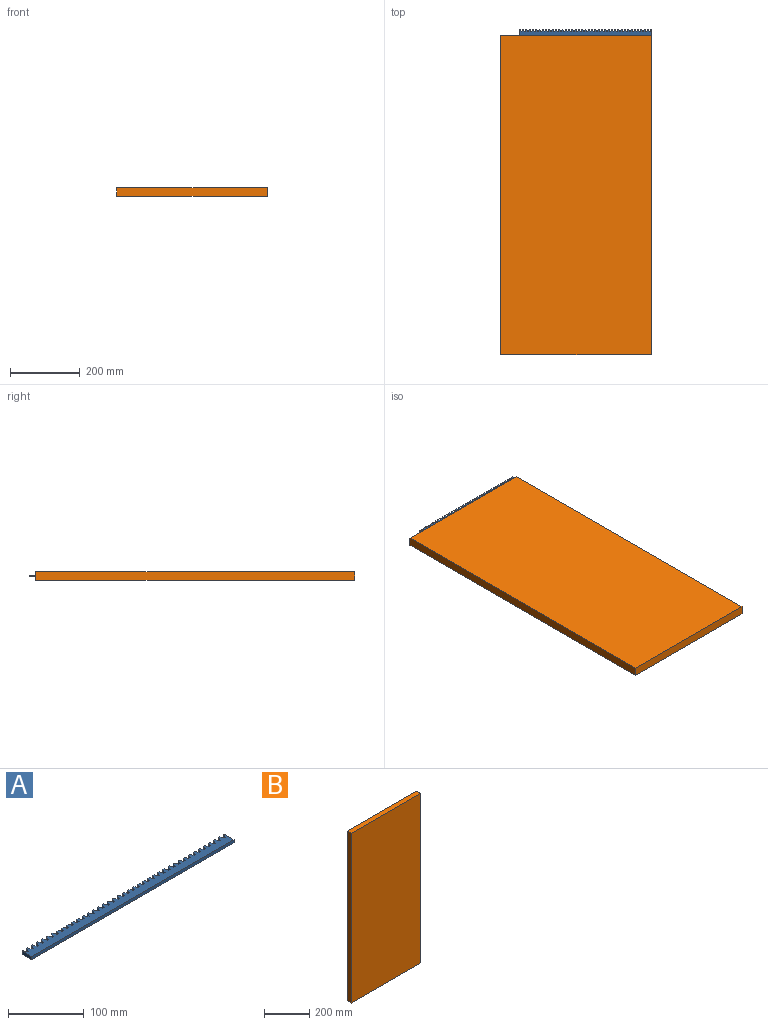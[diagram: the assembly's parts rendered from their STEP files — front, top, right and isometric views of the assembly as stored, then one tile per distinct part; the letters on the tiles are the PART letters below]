
ASSEMBLY  parts=2 mates=1
PART A: 166 faces, bbox 377x18x5 mm
  f0: plane 18x5mm, normal (-1,0,0), area 90mm2, adj f1,f4,f5,f6
  f1: plane 376.99x5mm, normal (0,-1,0), area 1885mm2, adj f0,f5,f6,f163
  f2: plane 5x2.53mm, normal (0,1,0), area 12.6mm2, adj f3,f5,f6,f7
  f3: plane 6x5mm, normal (0.94,0.34,0), area 31.9mm2, adj f2,f4,f5,f6
  f4: plane 5x1.26mm, normal (0,1,0), area 6.3mm2, adj f0,f3,f5,f6
  f5: plane 376.99x18mm, normal (0,0,1), area 5654.9mm2, adj f0,f1,f2,f3,f4,f7,f8,f9
  f6: plane 376.99x18mm, normal (0,0,-1), area 5654.9mm2, adj f0,f1,f2,f3,f4,f7,f8,f9
  f7: plane 6x5mm, normal (-0.94,0.34,0), area 31.9mm2, adj f2,f5,f6,f8
  f8: plane 5x2.53mm, normal (0,1,0), area 12.6mm2, adj f5,f6,f7,f10
  f9: plane 5x2.53mm, normal (0,1,0), area 12.6mm2, adj f5,f6,f10,f11
  f10: plane 6x5mm, normal (0.94,0.34,0), area 31.9mm2, adj f5,f6,f8,f9
  f11: plane 6x5mm, normal (-0.94,0.34,0), area 31.9mm2, adj f5,f6,f9,f12
  f12: plane 5x2.53mm, normal (0,1,0), area 12.6mm2, adj f5,f6,f11,f14
  f13: plane 5x2.53mm, normal (0,1,0), area 12.6mm2, adj f5,f6,f14,f15
  f14: plane 6x5mm, normal (0.94,0.34,0), area 31.9mm2, adj f5,f6,f12,f13
  f15: plane 6x5mm, normal (-0.94,0.34,0), area 31.9mm2, adj f5,f6,f13,f16
  f16: plane 5x2.53mm, normal (0,1,0), area 12.6mm2, adj f5,f6,f15,f18
  f17: plane 5x2.53mm, normal (0,1,0), area 12.6mm2, adj f5,f6,f18,f19
  f18: plane 6x5mm, normal (0.94,0.34,0), area 31.9mm2, adj f5,f6,f16,f17
  f19: plane 6x5mm, normal (-0.94,0.34,0), area 31.9mm2, adj f5,f6,f17,f20
  f20: plane 5x2.53mm, normal (0,1,0), area 12.6mm2, adj f5,f6,f19,f22
  f21: plane 5x2.53mm, normal (0,1,0), area 12.6mm2, adj f5,f6,f22,f23
  f22: plane 6x5mm, normal (0.94,0.34,0), area 31.9mm2, adj f5,f6,f20,f21
  f23: plane 6x5mm, normal (-0.94,0.34,0), area 31.9mm2, adj f5,f6,f21,f24
  f24: plane 5x2.53mm, normal (0,1,0), area 12.6mm2, adj f5,f6,f23,f26
  f25: plane 5x2.53mm, normal (0,1,0), area 12.6mm2, adj f5,f6,f26,f27
  f26: plane 6x5mm, normal (0.94,0.34,0), area 31.9mm2, adj f5,f6,f24,f25
  f27: plane 6x5mm, normal (-0.94,0.34,0), area 31.9mm2, adj f5,f6,f25,f28
  f28: plane 5x2.53mm, normal (0,1,0), area 12.6mm2, adj f5,f6,f27,f30
  f29: plane 5x2.53mm, normal (0,1,0), area 12.6mm2, adj f5,f6,f30,f31
  f30: plane 6x5mm, normal (0.94,0.34,0), area 31.9mm2, adj f5,f6,f28,f29
  f31: plane 6x5mm, normal (-0.94,0.34,0), area 31.9mm2, adj f5,f6,f29,f32
  f32: plane 5x2.53mm, normal (0,1,0), area 12.6mm2, adj f5,f6,f31,f34
  f33: plane 5x2.53mm, normal (0,1,0), area 12.6mm2, adj f5,f6,f34,f35
  f34: plane 6x5mm, normal (0.94,0.34,0), area 31.9mm2, adj f5,f6,f32,f33
  f35: plane 6x5mm, normal (-0.94,0.34,0), area 31.9mm2, adj f5,f6,f33,f36
  f36: plane 5x2.53mm, normal (0,1,0), area 12.6mm2, adj f5,f6,f35,f38
  f37: plane 5x2.53mm, normal (0,1,0), area 12.6mm2, adj f5,f6,f38,f39
  f38: plane 6x5mm, normal (0.94,0.34,0), area 31.9mm2, adj f5,f6,f36,f37
  f39: plane 6x5mm, normal (-0.94,0.34,0), area 31.9mm2, adj f5,f6,f37,f40
  f40: plane 5x2.53mm, normal (0,1,0), area 12.6mm2, adj f5,f6,f39,f42
  f41: plane 5x2.53mm, normal (0,1,0), area 12.6mm2, adj f5,f6,f42,f43
  f42: plane 6x5mm, normal (0.94,0.34,0), area 31.9mm2, adj f5,f6,f40,f41
  f43: plane 6x5mm, normal (-0.94,0.34,0), area 31.9mm2, adj f5,f6,f41,f44
  f44: plane 5x2.53mm, normal (0,1,0), area 12.6mm2, adj f5,f6,f43,f46
  f45: plane 5x2.53mm, normal (0,1,0), area 12.6mm2, adj f5,f6,f46,f47
  f46: plane 6x5mm, normal (0.94,0.34,0), area 31.9mm2, adj f5,f6,f44,f45
  f47: plane 6x5mm, normal (-0.94,0.34,0), area 31.9mm2, adj f5,f6,f45,f48
  f48: plane 5x2.53mm, normal (0,1,0), area 12.6mm2, adj f5,f6,f47,f50
  f49: plane 5x2.53mm, normal (0,1,0), area 12.6mm2, adj f5,f6,f50,f51
  f50: plane 6x5mm, normal (0.94,0.34,0), area 31.9mm2, adj f5,f6,f48,f49
  f51: plane 6x5mm, normal (-0.94,0.34,0), area 31.9mm2, adj f5,f6,f49,f52
  f52: plane 5x2.53mm, normal (0,1,0), area 12.6mm2, adj f5,f6,f51,f54
  f53: plane 5x2.53mm, normal (0,1,0), area 12.6mm2, adj f5,f6,f54,f55
  f54: plane 6x5mm, normal (0.94,0.34,0), area 31.9mm2, adj f5,f6,f52,f53
  f55: plane 6x5mm, normal (-0.94,0.34,0), area 31.9mm2, adj f5,f6,f53,f56
  f56: plane 5x2.53mm, normal (0,1,0), area 12.6mm2, adj f5,f6,f55,f58
  f57: plane 5x2.53mm, normal (0,1,0), area 12.6mm2, adj f5,f6,f58,f59
  f58: plane 6x5mm, normal (0.94,0.34,0), area 31.9mm2, adj f5,f6,f56,f57
  f59: plane 6x5mm, normal (-0.94,0.34,0), area 31.9mm2, adj f5,f6,f57,f60
  f60: plane 5x2.53mm, normal (0,1,0), area 12.6mm2, adj f5,f6,f59,f62
  f61: plane 5x2.53mm, normal (0,1,0), area 12.6mm2, adj f5,f6,f62,f63
  f62: plane 6x5mm, normal (0.94,0.34,0), area 31.9mm2, adj f5,f6,f60,f61
  f63: plane 6x5mm, normal (-0.94,0.34,0), area 31.9mm2, adj f5,f6,f61,f64
  f64: plane 5x2.53mm, normal (0,1,0), area 12.6mm2, adj f5,f6,f63,f66
  f65: plane 5x2.53mm, normal (0,1,0), area 12.6mm2, adj f5,f6,f66,f67
  f66: plane 6x5mm, normal (0.94,0.34,0), area 31.9mm2, adj f5,f6,f64,f65
  f67: plane 6x5mm, normal (-0.94,0.34,0), area 31.9mm2, adj f5,f6,f65,f68
  f68: plane 5x2.53mm, normal (0,1,0), area 12.6mm2, adj f5,f6,f67,f70
  f69: plane 5x2.53mm, normal (0,1,0), area 12.6mm2, adj f5,f6,f70,f71
  f70: plane 6x5mm, normal (0.94,0.34,0), area 31.9mm2, adj f5,f6,f68,f69
  f71: plane 6x5mm, normal (-0.94,0.34,0), area 31.9mm2, adj f5,f6,f69,f72
  f72: plane 5x2.53mm, normal (0,1,0), area 12.6mm2, adj f5,f6,f71,f74
  f73: plane 5x2.53mm, normal (0,1,0), area 12.6mm2, adj f5,f6,f74,f75
  f74: plane 6x5mm, normal (0.94,0.34,0), area 31.9mm2, adj f5,f6,f72,f73
  f75: plane 6x5mm, normal (-0.94,0.34,0), area 31.9mm2, adj f5,f6,f73,f76
  f76: plane 5x2.53mm, normal (0,1,0), area 12.6mm2, adj f5,f6,f75,f78
  f77: plane 5x2.53mm, normal (0,1,0), area 12.6mm2, adj f5,f6,f78,f79
  f78: plane 6x5mm, normal (0.94,0.34,0), area 31.9mm2, adj f5,f6,f76,f77
  f79: plane 6x5mm, normal (-0.94,0.34,0), area 31.9mm2, adj f5,f6,f77,f80
  f80: plane 5x2.53mm, normal (0,1,0), area 12.6mm2, adj f5,f6,f79,f82
  f81: plane 5x2.53mm, normal (0,1,0), area 12.6mm2, adj f5,f6,f82,f83
  f82: plane 6x5mm, normal (0.94,0.34,0), area 31.9mm2, adj f5,f6,f80,f81
  f83: plane 6x5mm, normal (-0.94,0.34,0), area 31.9mm2, adj f5,f6,f81,f84
  f84: plane 5x2.53mm, normal (0,1,0), area 12.6mm2, adj f5,f6,f83,f86
  f85: plane 5x2.53mm, normal (0,1,0), area 12.6mm2, adj f5,f6,f86,f87
  f86: plane 6x5mm, normal (0.94,0.34,0), area 31.9mm2, adj f5,f6,f84,f85
  f87: plane 6x5mm, normal (-0.94,0.34,0), area 31.9mm2, adj f5,f6,f85,f88
  f88: plane 5x2.53mm, normal (0,1,0), area 12.6mm2, adj f5,f6,f87,f90
  f89: plane 5x2.53mm, normal (0,1,0), area 12.6mm2, adj f5,f6,f90,f91
  f90: plane 6x5mm, normal (0.94,0.34,0), area 31.9mm2, adj f5,f6,f88,f89
  f91: plane 6x5mm, normal (-0.94,0.34,0), area 31.9mm2, adj f5,f6,f89,f92
  f92: plane 5x2.53mm, normal (0,1,0), area 12.6mm2, adj f5,f6,f91,f94
  f93: plane 5x2.53mm, normal (0,1,0), area 12.6mm2, adj f5,f6,f94,f95
  f94: plane 6x5mm, normal (0.94,0.34,0), area 31.9mm2, adj f5,f6,f92,f93
  f95: plane 6x5mm, normal (-0.94,0.34,0), area 31.9mm2, adj f5,f6,f93,f96
  f96: plane 5x2.53mm, normal (0,1,0), area 12.6mm2, adj f5,f6,f95,f98
  f97: plane 5x2.53mm, normal (0,1,0), area 12.6mm2, adj f5,f6,f98,f99
  f98: plane 6x5mm, normal (0.94,0.34,0), area 31.9mm2, adj f5,f6,f96,f97
  f99: plane 6x5mm, normal (-0.94,0.34,0), area 31.9mm2, adj f5,f6,f97,f100
  f100: plane 5x2.53mm, normal (0,1,0), area 12.6mm2, adj f5,f6,f99,f102
  f101: plane 5x2.53mm, normal (0,1,0), area 12.6mm2, adj f5,f6,f102,f103
  f102: plane 6x5mm, normal (0.94,0.34,0), area 31.9mm2, adj f5,f6,f100,f101
  f103: plane 6x5mm, normal (-0.94,0.34,0), area 31.9mm2, adj f5,f6,f101,f104
  f104: plane 5x2.53mm, normal (0,1,0), area 12.6mm2, adj f5,f6,f103,f106
  f105: plane 5x2.53mm, normal (0,1,0), area 12.6mm2, adj f5,f6,f106,f107
  f106: plane 6x5mm, normal (0.94,0.34,0), area 31.9mm2, adj f5,f6,f104,f105
  f107: plane 6x5mm, normal (-0.94,0.34,0), area 31.9mm2, adj f5,f6,f105,f108
  f108: plane 5x2.53mm, normal (0,1,0), area 12.6mm2, adj f5,f6,f107,f110
  f109: plane 5x2.53mm, normal (0,1,0), area 12.6mm2, adj f5,f6,f110,f111
  f110: plane 6x5mm, normal (0.94,0.34,0), area 31.9mm2, adj f5,f6,f108,f109
  f111: plane 6x5mm, normal (-0.94,0.34,0), area 31.9mm2, adj f5,f6,f109,f112
  f112: plane 5x2.53mm, normal (0,1,0), area 12.6mm2, adj f5,f6,f111,f114
  f113: plane 5x2.53mm, normal (0,1,0), area 12.6mm2, adj f5,f6,f114,f115
  f114: plane 6x5mm, normal (0.94,0.34,0), area 31.9mm2, adj f5,f6,f112,f113
  f115: plane 6x5mm, normal (-0.94,0.34,0), area 31.9mm2, adj f5,f6,f113,f116
  f116: plane 5x2.53mm, normal (0,1,0), area 12.6mm2, adj f5,f6,f115,f118
  f117: plane 5x2.53mm, normal (0,1,0), area 12.6mm2, adj f5,f6,f118,f119
  f118: plane 6x5mm, normal (0.94,0.34,0), area 31.9mm2, adj f5,f6,f116,f117
  f119: plane 6x5mm, normal (-0.94,0.34,0), area 31.9mm2, adj f5,f6,f117,f120
  f120: plane 5x2.53mm, normal (0,1,0), area 12.6mm2, adj f5,f6,f119,f122
  f121: plane 5x2.53mm, normal (0,1,0), area 12.6mm2, adj f5,f6,f122,f123
  f122: plane 6x5mm, normal (0.94,0.34,0), area 31.9mm2, adj f5,f6,f120,f121
  f123: plane 6x5mm, normal (-0.94,0.34,0), area 31.9mm2, adj f5,f6,f121,f124
  f124: plane 5x2.53mm, normal (0,1,0), area 12.6mm2, adj f5,f6,f123,f126
  f125: plane 5x2.53mm, normal (0,1,0), area 12.6mm2, adj f5,f6,f126,f127
  f126: plane 6x5mm, normal (0.94,0.34,0), area 31.9mm2, adj f5,f6,f124,f125
  f127: plane 6x5mm, normal (-0.94,0.34,0), area 31.9mm2, adj f5,f6,f125,f128
  f128: plane 5x2.53mm, normal (0,1,0), area 12.6mm2, adj f5,f6,f127,f130
  f129: plane 5x2.53mm, normal (0,1,0), area 12.6mm2, adj f5,f6,f130,f131
  f130: plane 6x5mm, normal (0.94,0.34,0), area 31.9mm2, adj f5,f6,f128,f129
  f131: plane 6x5mm, normal (-0.94,0.34,0), area 31.9mm2, adj f5,f6,f129,f132
  f132: plane 5x2.53mm, normal (0,1,0), area 12.6mm2, adj f5,f6,f131,f134
  f133: plane 5x2.53mm, normal (0,1,0), area 12.6mm2, adj f5,f6,f134,f135
  f134: plane 6x5mm, normal (0.94,0.34,0), area 31.9mm2, adj f5,f6,f132,f133
  f135: plane 6x5mm, normal (-0.94,0.34,0), area 31.9mm2, adj f5,f6,f133,f136
  f136: plane 5x2.53mm, normal (0,1,0), area 12.6mm2, adj f5,f6,f135,f138
  f137: plane 5x2.53mm, normal (0,1,0), area 12.6mm2, adj f5,f6,f138,f139
  f138: plane 6x5mm, normal (0.94,0.34,0), area 31.9mm2, adj f5,f6,f136,f137
  f139: plane 6x5mm, normal (-0.94,0.34,0), area 31.9mm2, adj f5,f6,f137,f140
  f140: plane 5x2.53mm, normal (0,1,0), area 12.6mm2, adj f5,f6,f139,f142
  f141: plane 5x2.53mm, normal (0,1,0), area 12.6mm2, adj f5,f6,f142,f143
  f142: plane 6x5mm, normal (0.94,0.34,0), area 31.9mm2, adj f5,f6,f140,f141
  f143: plane 6x5mm, normal (-0.94,0.34,0), area 31.9mm2, adj f5,f6,f141,f144
  f144: plane 5x2.53mm, normal (0,1,0), area 12.6mm2, adj f5,f6,f143,f146
  f145: plane 5x2.53mm, normal (0,1,0), area 12.6mm2, adj f5,f6,f146,f147
  f146: plane 6x5mm, normal (0.94,0.34,0), area 31.9mm2, adj f5,f6,f144,f145
  f147: plane 6x5mm, normal (-0.94,0.34,0), area 31.9mm2, adj f5,f6,f145,f148
  f148: plane 5x2.53mm, normal (0,1,0), area 12.6mm2, adj f5,f6,f147,f150
  f149: plane 5x2.53mm, normal (0,1,0), area 12.6mm2, adj f5,f6,f150,f151
  f150: plane 6x5mm, normal (0.94,0.34,0), area 31.9mm2, adj f5,f6,f148,f149
  f151: plane 6x5mm, normal (-0.94,0.34,0), area 31.9mm2, adj f5,f6,f149,f152
  f152: plane 5x2.53mm, normal (0,1,0), area 12.6mm2, adj f5,f6,f151,f154
  f153: plane 5x2.53mm, normal (0,1,0), area 12.6mm2, adj f5,f6,f154,f155
  f154: plane 6x5mm, normal (0.94,0.34,0), area 31.9mm2, adj f5,f6,f152,f153
  f155: plane 6x5mm, normal (-0.94,0.34,0), area 31.9mm2, adj f5,f6,f153,f156
  f156: plane 5x2.53mm, normal (0,1,0), area 12.6mm2, adj f5,f6,f155,f158
  f157: plane 5x2.53mm, normal (0,1,0), area 12.6mm2, adj f5,f6,f158,f159
  f158: plane 6x5mm, normal (0.94,0.34,0), area 31.9mm2, adj f5,f6,f156,f157
  f159: plane 6x5mm, normal (-0.94,0.34,0), area 31.9mm2, adj f5,f6,f157,f160
  f160: plane 5x2.53mm, normal (0,1,0), area 12.6mm2, adj f5,f6,f159,f162
  f161: plane 5x2.53mm, normal (0,1,0), area 12.6mm2, adj f5,f6,f162,f164
  f162: plane 6x5mm, normal (0.94,0.34,0), area 31.9mm2, adj f5,f6,f160,f161
  f163: plane 18x5mm, normal (1,0,0), area 90mm2, adj f1,f5,f6,f165
  f164: plane 6x5mm, normal (-0.94,0.34,0), area 31.9mm2, adj f5,f6,f161,f165
  f165: plane 5x1.26mm, normal (0,1,0), area 6.3mm2, adj f5,f6,f163,f164
PART B: 6 faces, bbox 431.8x25.4x914.4 mm
  f0: plane 431.8x25.4mm, normal (0,0,-1), area 10967.7mm2, adj f1,f3,f4,f5
  f1: plane 914.4x25.4mm, normal (1,0,0), area 23225.8mm2, adj f0,f2,f4,f5
  f2: plane 431.8x25.4mm, normal (0,0,1), area 10967.7mm2, adj f1,f3,f4,f5
  f3: plane 914.4x25.4mm, normal (-1,0,0), area 23225.8mm2, adj f0,f2,f4,f5
  f4: plane 914.4x431.8mm, normal (0,-1,0), area 394837.9mm2, adj f0,f1,f2,f3
  f5: plane 914.4x431.8mm, normal (0,1,0), area 394837.9mm2, adj f0,f1,f2,f3
PLACE A at identity
PLACE B rot(axis=(-1,0,0),90deg) t=(339.29,-929.4,-10.2)mm
MATE fastened B.f2 <-> A.f1  axis (0,1,0) through (339.29,-15,2.5)mm
